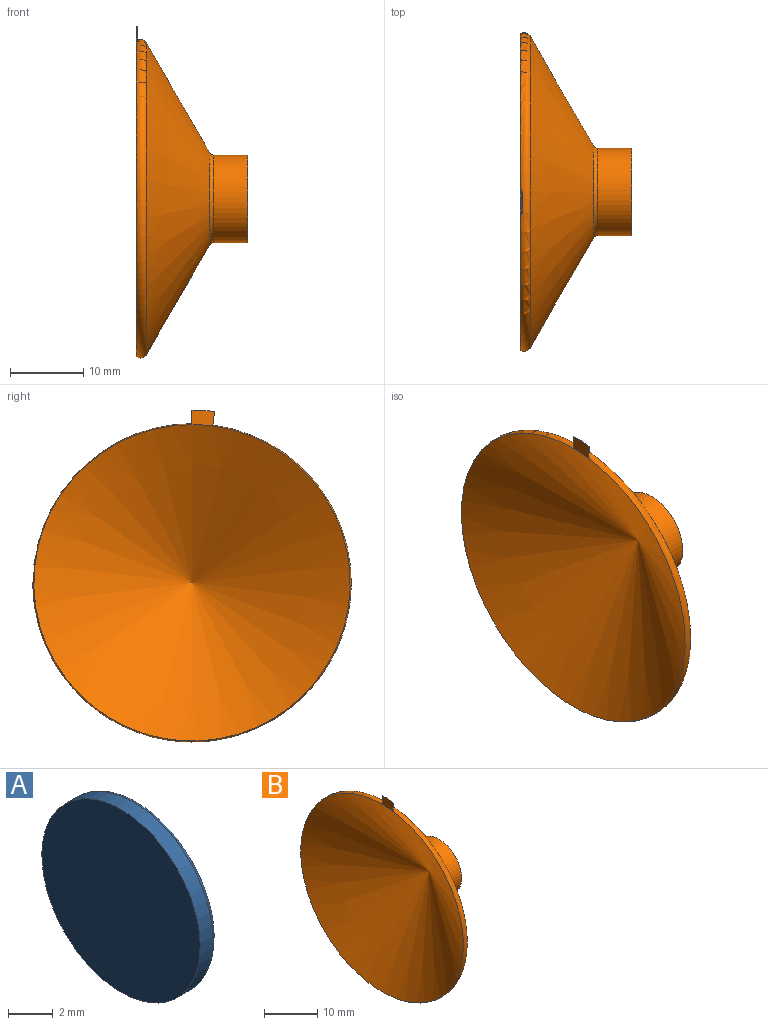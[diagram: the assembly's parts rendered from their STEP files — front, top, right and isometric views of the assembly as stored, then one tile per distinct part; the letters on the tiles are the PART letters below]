
ASSEMBLY  parts=2 mates=1
PART A: 7 faces, bbox 1.5x10.8x10.8 mm
  f0: cylinder r=5mm len=10mm, axis (-1,0,0), area 25.1mm2, adj f2,f6
  f1: plane 9.6x9.6mm, normal (1,0,0), area 22.1mm2, adj f3,f6
  f2: plane 10x10mm, normal (-1,0,0), area 78.5mm2, adj f0
  f3: cylinder r=4mm len=8mm, axis (-1,0,0), area 7.5mm2, adj f1,f5
  f4: plane 7.6x7.6mm, normal (1,0,0), area 45.4mm2, adj f5
  f5: torus R=3.8mm, axis (1,0,0), area 7.8mm2, adj f3,f4
  f6: torus R=4.8mm, axis (1,0,0), area 9.7mm2, adj f0,f1
PART B: 18 faces, bbox 15.4x47.2x47.3 mm
  f0: torus R=20.78mm, axis (-1,0,0), area 213mm2, adj f1,f8,f14,f15,f16
  f1: cone r=0mm half-angle=60deg, axis (-1,0,0), area 1700.4mm2, adj f0,f11
  f2: plane 10x10mm, normal (1,0,0), area 78.5mm2, adj f3
  f3: cylinder r=5mm len=10mm, axis (1,0,0), area 31.4mm2, adj f2,f4
  f4: plane 10x10mm, normal (-1,0,0), area 28.3mm2, adj f3,f5
  f5: cylinder r=4mm len=8mm, axis (1,0,0), area 12.6mm2, adj f4,f6
  f6: plane 12x12mm, normal (1,0,0), area 62.8mm2, adj f5,f7
  f7: cylinder r=6mm len=12mm, axis (1,0,0), area 177.6mm2, adj f6,f9
  f8: cone r=23.65mm half-angle=60deg, axis (-1,0,0), area 1501.7mm2, adj f0,f9
  f9: torus R=6.5mm, axis (1,0,0), area 20mm2, adj f7,f8
  f10: plane 3.07x1.89mm, normal (1,0,0), area 5.1mm2, adj f12,f13,f16,f17
  f11: plane 3.21x2.22mm, normal (-1,0,0), area 5.9mm2, adj f1,f12,f13,f14,f15,f17
  f12: plane 1.87x0.25mm, normal (0,-0.99,-0.13), area 0.2mm2, adj f10,f11,f14,f16,f17
  f13: plane 1.89x0.11mm, normal (0,1,0), area 0.2mm2, adj f10,f11,f15,f16,f17
  f14: bspline ~0.57x0.33mm, area 0mm2, adj f0,f11,f12,f16
  f15: bspline ~0.57x0.32mm, area 0mm2, adj f0,f11,f13,f16
  f16: torus R=21.84mm, axis (1,0,0), area 0.5mm2, adj f0,f10,f12,f13,f14,f15
  f17: torus R=23.55mm, axis (1,0,0), area 0.5mm2, adj f10,f11,f12,f13
PLACE A t=(-16.33,7.06,24.64)mm
PLACE B t=(-30.02,7.06,48.29)mm
MATE fastened B.f0 <-> A.f0  axis (1,0,0) through (-16.33,7.06,24.64)mm
